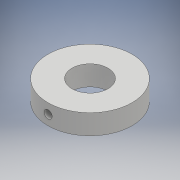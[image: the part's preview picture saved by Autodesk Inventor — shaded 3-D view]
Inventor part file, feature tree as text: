
AUTODESK INVENTOR PART (.ipt)
format: ipt  version: 2018 (Build 220112000, 112)  size: 106,496 bytes
history: native  units: mm
features: extrude x2, sketch x2
ambient origin geometry x8: Origin, YZ Plane, XZ Plane, XY Plane, X Axis, Y Axis, Z Axis, Center Point
bodies: Solid1 (feature_tree)
feature tree (4):
  extrude  "Extrusion1"  Depth=6.0mm
  extrude  "Extrusion2"  Depth=2.0mm
  sketch  "Sketch1"  dims[d0=9.0mm d1=6.0mm]
  sketch  "Sketch2"  dims[d2=5.0mm d3=0.0mm d4=2.0mm d5=6.0mm d6=0.0mm]
